# Revit family: 1
name_source: partatom
category: Pipe Accessories
revit_build: Autodesk Revit 2018 (Build: 20190510_1515(x64)
units: mm (PartAtom-declared; Revit-internal decimal feet)

## family parameters
Always vertical = No
Cut with Voids When Loaded = No
OmniClass Number = 23.65.00.00
OmniClass Title = Supply and Distribution of Liquids and Gases
Part Type = Normal
Round Connector Dimension = Use Diameter
Shared = No
Work Plane-Based = No

## types (2) — shared parameters
Antifreeze: = Passiveted Propylene Glycol
Application fluids = Water or glycol solutions
BIMobject category = Plumbing Valves
Brand url = www.pintossi.it
Conditioning: = as indicated by the producer
Copper (CU): = < 0,1 mg/kg (< 0,05 mg/kg for steam)
Description = Pintossi+C automatic filling unit is installed in heating system to maintain stable the internal pressure at a set value, filling the circuit with water if required.

Pressure can drop following to air release caused by air separator or relief valves placed in the highest point of the system and on the radiators.

During this phase the check valve built-in the filling unit avoids backflows from the heating system to the water supply. When reaching the pre-set level, that can be read from the manometer on art. 513, the filling unit closes, avoiding damages caused by overpressure. When the system is in operation the valve works automatically.

The filling unit is provided with a shut-off cock which is actived by the handwheel placed on the lower part of the valve.

The cartridge containing the operation mechanism is protected by a large surface strainer.

Available with or without manometer.
Design country = Italy
Downstream adjustable pressure = 0,5 – 3bar
Fluid aspect: = Limpid
IFC Classification = Valve
Iron (FE): = < 0,5 mg/kg (< 0,1 mg/kg for steam)
Main Inlet/Outlet Diameter = 13 mm
Manometer scale (art. 562) = 0 – 4bar
Manufacturer = Pintossi+C
Manufacturer country = Italy
Manufacturer name = Pintossi+C
Masterformat 2014 Code = 23 00 00
Masterformat 2014 Description = Heating, Ventilating, and Air Conditioning (HVAC)
Material Body = Pintossi - Metal - Brass CW617N
Material Glass = Pintossi - Glass - Glass
Material Manometer Black = Pintossi - Plastic - Black ABS
Material Manometer White = Pintossi - Plastic - ABS
Material Protection Cap = Pintossi - Plastic - Grey ABS
Material main = Brass
Maximum percentage of glycol [%] = 30
Maximum working pressure = 10.0 bar
Maximum working temperature = 90 °C
Mixed water range = 27 °C - 55 °C
Model = 1/2" - With manometer
NBS Reference Code = 94-94-xx
NBS Reference Description = Pressure Reducing Valves
OmniClass Code = 23-27 31 00
OmniClass Description = Valves
PH: = Between 7 and 8Between 7 and 8
Product Guid = 62f35bb9-9d1e-4464-84b0-297bad8f7bb6
Product SKU = 513-AUTOMATIC-FILLING-UNIT
Product data url = https://www.bimobject.com
Product family = COMPONENTS FOR CENTRAL HEATING SYSTEMS
Product group = THERMOSTATIC MIXING VALVES
UNSPSC Code = 401416
URL = www.pintossi.it
Uniclass 1.4 Code = JT10
Uniclass 1.4 Description = Heating systems
Uniclass 2.0 Code = PR-94-94-xx
Uniclass 2.0 Description = Thermostatic Mixing Valves
Uniclass 2015 Code = Pr_65_54_95_66
Uniclass 2015 Name = Pressure reducing valves
Uniformat II Code = D30
Uniformat II Description = HVAC
Weight Net (Kg) = 0
zero-valued in all types: Edition number

## per-type parameters (varying)
| type | With manometer |
| 1/2" - With manometer | Yes |
| 1/2" - Without manometer | No |

## geometry (parser evidence)
native form markers: Sweep x2
no freeform markers — native parametric forms only
